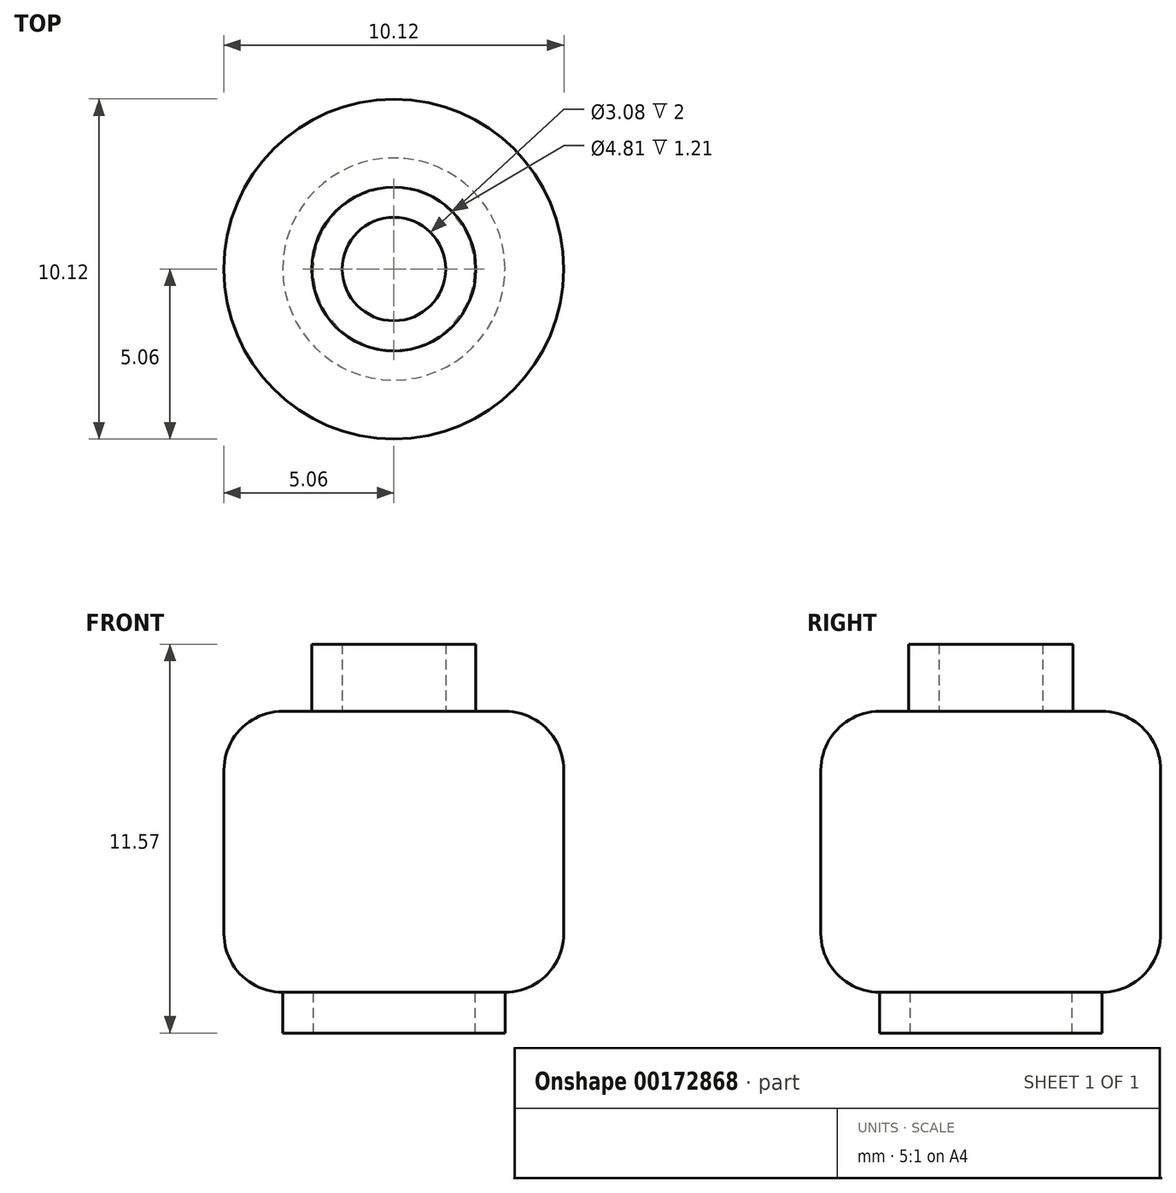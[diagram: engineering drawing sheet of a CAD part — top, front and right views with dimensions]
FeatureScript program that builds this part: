
annotation { "Feature Type Name" : "Feature", "Feature Type Description" : "" }
export const myFeature = defineFeature(function(context is Context, id is Id, definition is map)
    precondition{}
    {
        {
            var Q0;
            Q0=qCreatedBy(makeId("Front.planeOp"),FACE);
            var sketch = newSketch(context, id + "F0", { "sketchPlane" : qUnion([Q0])});
            skLineSegment(sketch, "E0", {"start": v(0, 0) * mm, "end": v(0, 56.1) * mm, "construction": true});
            skLineSegment(sketch, "E1", {"start": v(1.54, 0) * mm, "end": v(2.44, 0) * mm});
            skLineSegment(sketch, "E2", {"start": v(1.54, 0) * mm, "end": v(1.54, -2) * mm});
            skLineSegment(sketch, "E3", {"start": v(0, 0) * mm, "end": v(0, -48.5) * mm, "construction": true});
            skLineSegment(sketch, "E4", {"start": v(1.54, -2) * mm, "end": v(0, -2) * mm});
            skLineSegment(sketch, "E5", {"start": v(0, -2) * mm, "end": v(0, -10.36) * mm});
            skLineSegment(sketch, "E6", {"start": v(2.44, 0) * mm, "end": v(2.44, -2) * mm});
            skLineSegment(sketch, "E7", {"start": v(2.44, -2) * mm, "end": v(3.3, -2) * mm});
            skArc(sketch, "E8", {"start": v(5.05, -3.75) * mm, "mid": v(4.54, -2.51) * mm, "end": v(3.3, -2) * mm});
            skLineSegment(sketch, "E9", {"start": v(5.06, -3.75) * mm, "end": v(5.06, -8.6) * mm});
            skArc(sketch, "E10", {"start": v(3.3, -10.36) * mm, "mid": v(4.54, -9.85) * mm, "end": v(5.06, -8.6) * mm});
            skLineSegment(sketch, "E11", {"start": v(3.3, -10.36) * mm, "end": v(3.3, -11.57) * mm});
            skLineSegment(sketch, "E12", {"start": v(3.3, -11.57) * mm, "end": v(2.4, -11.57) * mm});
            skLineSegment(sketch, "E13", {"start": v(2.4, -11.57) * mm, "end": v(2.4, -10.36) * mm});
            skLineSegment(sketch, "E14", {"start": v(2.4, -10.36) * mm, "end": v(0, -10.36) * mm});
            skSolve(sketch);
        }
        {
            var Q0;
            Q0 = qSketchRegion(id + "F0", true);
            var Q1;
            Q1=sQuery(id+"F0.wireOp",EDGE,"E0");
            revolve(context, id + "F1", {"entities" : qUnion([Q0]), "axis" : qUnion([Q1]), "revolveType" : RevolveType.FULL});
        }
    });
